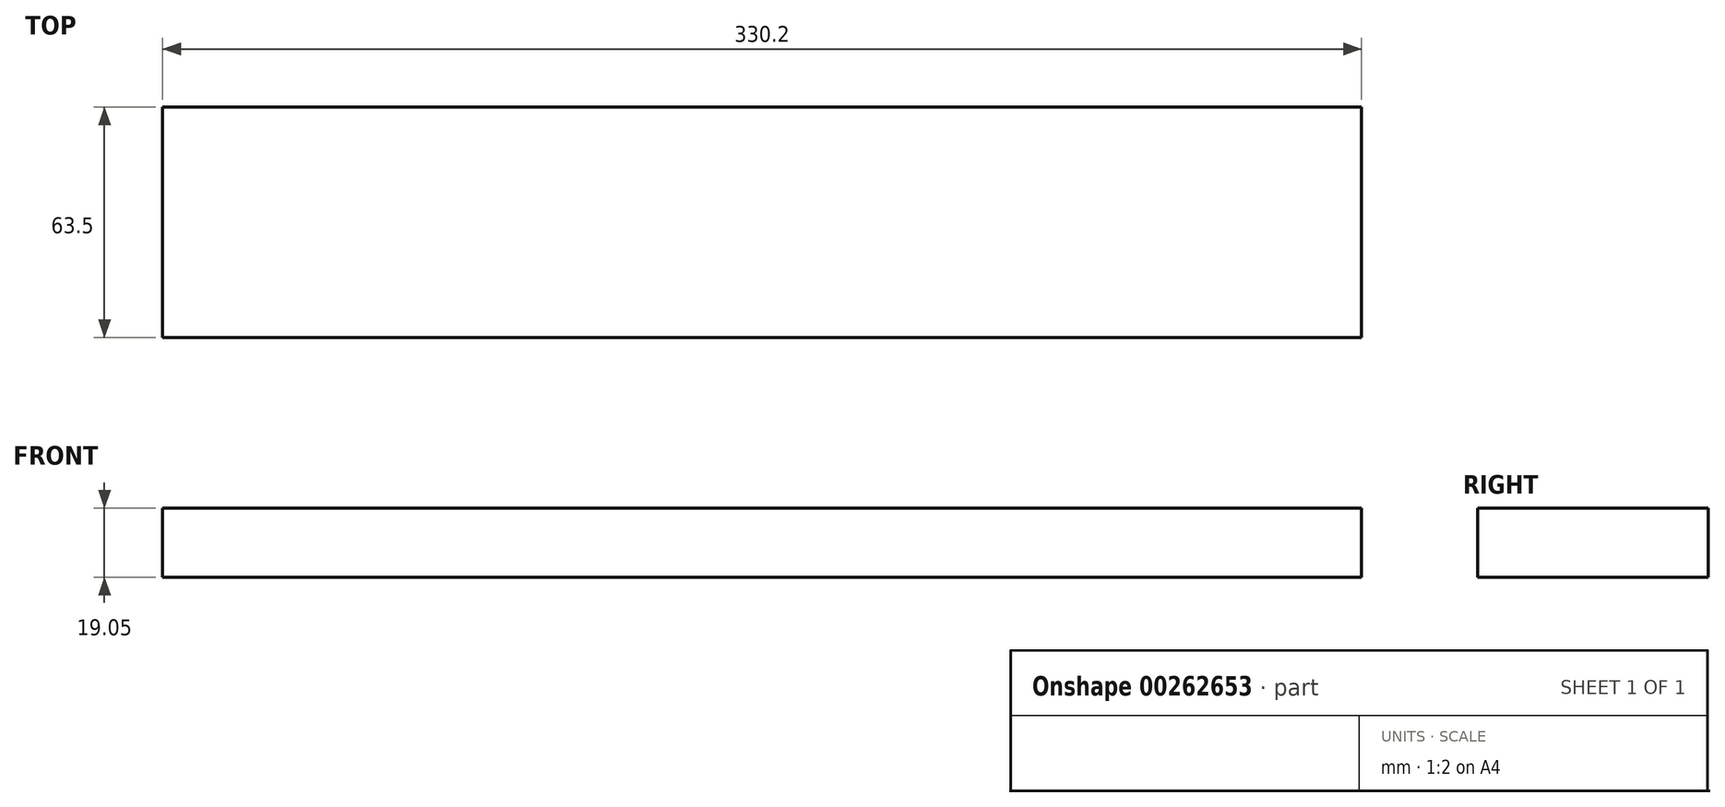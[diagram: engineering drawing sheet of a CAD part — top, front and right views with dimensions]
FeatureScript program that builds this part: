
annotation { "Feature Type Name" : "Feature", "Feature Type Description" : "" }
export const myFeature = defineFeature(function(context is Context, id is Id, definition is map)
    precondition{}
    {
        {
            var Q0;
            Q0=qCreatedBy(makeId("Top.planeOp"),FACE);
            var sketch = newSketch(context, id + "F0", { "sketchPlane" : qUnion([Q0])});
            skLineSegment(sketch, "E0.bottom", {"start": v(0, 0) * mm, "end": v(330.2, 0) * mm});
            skLineSegment(sketch, "E0.top", {"start": v(0, 63.5) * mm, "end": v(330.2, 63.5) * mm});
            skLineSegment(sketch, "E0.left", {"start": v(0, 0) * mm, "end": v(0, 63.5) * mm});
            skLineSegment(sketch, "E0.right", {"start": v(330.2, 0) * mm, "end": v(330.2, 63.5) * mm});
            skSolve(sketch);
        }
        {
            var Q0;
            Q0=makeQuery(id+"F0.imprint","IMPRINT",FACE,{"disambiguationData":[TD([[makeQuery(id+"F0.imprint","IMPRINT",EDGE,{"derivedFrom":sQuery(id+"F0.wireOp",EDGE,"E0.bottom")}),1.0]])]});
            extrude(context, id + "F1", {"entities" : qUnion([Q0]), "depth" : 19.05 * mm, "offsetDistance" : 25.4 * mm});
        }
    });
